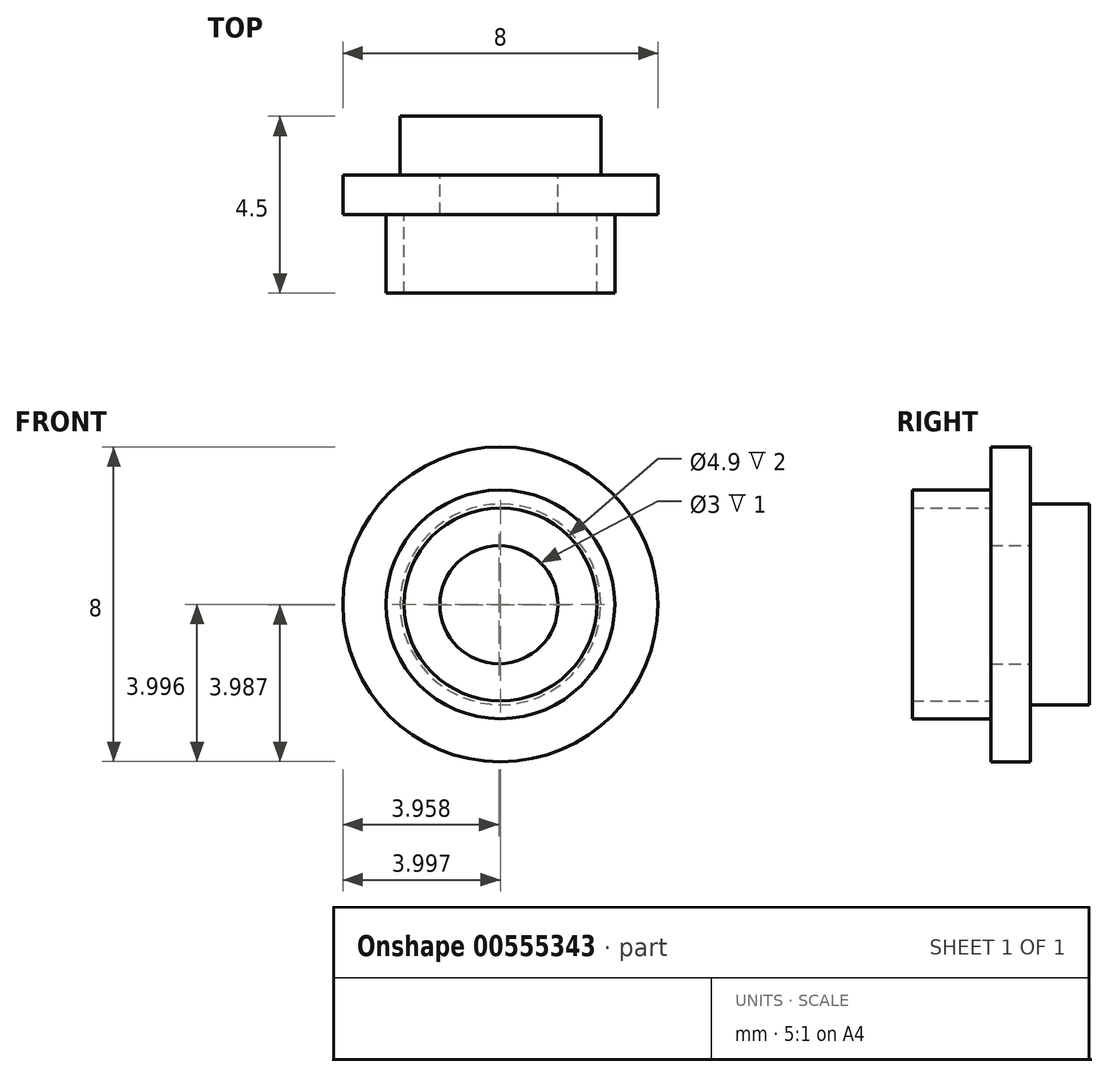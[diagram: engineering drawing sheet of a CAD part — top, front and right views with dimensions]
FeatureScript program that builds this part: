
annotation { "Feature Type Name" : "Feature", "Feature Type Description" : "" }
export const myFeature = defineFeature(function(context is Context, id is Id, definition is map)
    precondition{}
    {
        {
            var Q0;
            Q0=qCreatedBy(makeId("Front.planeOp"),FACE);
            var sketch = newSketch(context, id + "F0", { "sketchPlane" : qUnion([Q0])});
            skCircle(sketch, "E0", {"center": v(-18.85, 9.86) * mm, "radius": 4 * mm});
            skCircle(sketch, "E1", {"center": v(-18.85, 9.86) * mm, "radius": 3.5 * mm});
            skCircle(sketch, "E2", {"center": v(-18.85, 9.86) * mm, "radius": 3 * mm});
            skSolve(sketch);
        }
        {
            var Q0;
            Q0=makeQuery(id+"F0.imprint","IMPRINT",FACE,{"disambiguationData":[TD([[makeQuery(id+"F0.imprint","IMPRINT",EDGE,{"derivedFrom":sQuery(id+"F0.wireOp",EDGE,"E1")}),1.0]])]});
            var Q1;
            Q1=makeQuery(id+"F0.imprint","IMPRINT",FACE,{"disambiguationData":[TD([[makeQuery(id+"F0.imprint","IMPRINT",EDGE,{"derivedFrom":sQuery(id+"F0.wireOp",EDGE,"E0")}),1.0]])]});
            var Q2;
            Q2=makeQuery(id+"F0.imprint","IMPRINT",FACE,{"disambiguationData":[TD([[makeQuery(id+"F0.imprint","IMPRINT",EDGE,{"derivedFrom":sQuery(id+"F0.wireOp",EDGE,"E2")}),1.0]])]});
            extrude(context, id + "F1", {"entities" : qUnion([Q0, Q1, Q2]), "depth" : 1 * mm, "offsetDistance" : 25.4 * mm});
        }
        {
            var Q0;
            Q0=makeQuery(id+"F1.opExtrude","CAP_FACE",FACE,{"disambiguationData":[OSD([sQuery(id+"F0.wireOp",EDGE,"E0")])],"isStart":false});
            var sketch = newSketch(context, id + "F2", { "sketchPlane" : qUnion([Q0])});
            skCircle(sketch, "E3", {"center": v(-18.85, 9.86) * mm, "radius": 2.9 * mm});
            skCircle(sketch, "E4", {"center": v(-18.85, 9.86) * mm, "radius": 2.45 * mm});
            skSolve(sketch);
        }
        {
            var Q0;
            Q0=makeQuery(id+"F2.imprint","IMPRINT",FACE,{"disambiguationData":[TD([[makeQuery(id+"F2.imprint","IMPRINT",EDGE,{"derivedFrom":sQuery(id+"F2.wireOp",EDGE,"E3")}),1.0]])]});
            extrude(context, id + "F3", {"entities" : qUnion([Q0]), "operationType" : NewBodyOperationType.ADD, "depth" : 2 * mm, "offsetDistance" : 25.4 * mm});
        }
        {
            var Q0;
            Q0=makeQuery(id+"F1.opExtrude","CAP_FACE",FACE,{"disambiguationData":[OSD([sQuery(id+"F0.wireOp",EDGE,"E0")])],"isStart":true});
            var sketch = newSketch(context, id + "F4", { "sketchPlane" : qUnion([Q0])});
            skCircle(sketch, "E5", {"center": v(18.85, 9.86) * mm, "radius": 2.55 * mm});
            skSolve(sketch);
        }
        {
            var Q0;
            Q0=makeQuery(id+"F4.imprint","IMPRINT",FACE,{"disambiguationData":[TD([[makeQuery(id+"F4.imprint","IMPRINT",EDGE,{"derivedFrom":sQuery(id+"F4.wireOp",EDGE,"E5")}),1.0]])]});
            extrude(context, id + "F5", {"entities" : qUnion([Q0]), "operationType" : NewBodyOperationType.ADD, "depth" : 1.5 * mm, "offsetDistance" : 25.4 * mm});
        }
        {
            var Q0;
            Q0=qCreatedBy(makeId("Front.planeOp"),FACE);
            var sketch = newSketch(context, id + "F6", { "sketchPlane" : qUnion([Q0])});
            skCircle(sketch, "E6", {"center": v(-18.9, 9.85) * mm, "radius": 1.5 * mm});
            skSolve(sketch);
        }
        {
            var Q0;
            Q0=sQuery(id+"F6.wireOp",VERTEX,"E6.center");
            var Q1;
            Q1=makeQuery(id+"F1.opExtrude","SWEPT_BODY",BODY,{"disambiguationData":[OSD([sQuery(id+"F0.wireOp",EDGE,"E0")])]});
            hole(context, id + "F7", {"style" : HoleStyle.SIMPLE, "endStyle" : HoleEndStyle.BLIND, "oppositeDirection" : true, "holeDiameter" : 3 * mm, "holeDepth" : 2 * mm, "isTappedThrough" : true, "tappedDepth" : 12.7 * mm, "tapClearance" : 3, "startFromSketch" : true, "locations" : qUnion([Q0]), "scope" : qUnion([Q1])});
        }
    });
